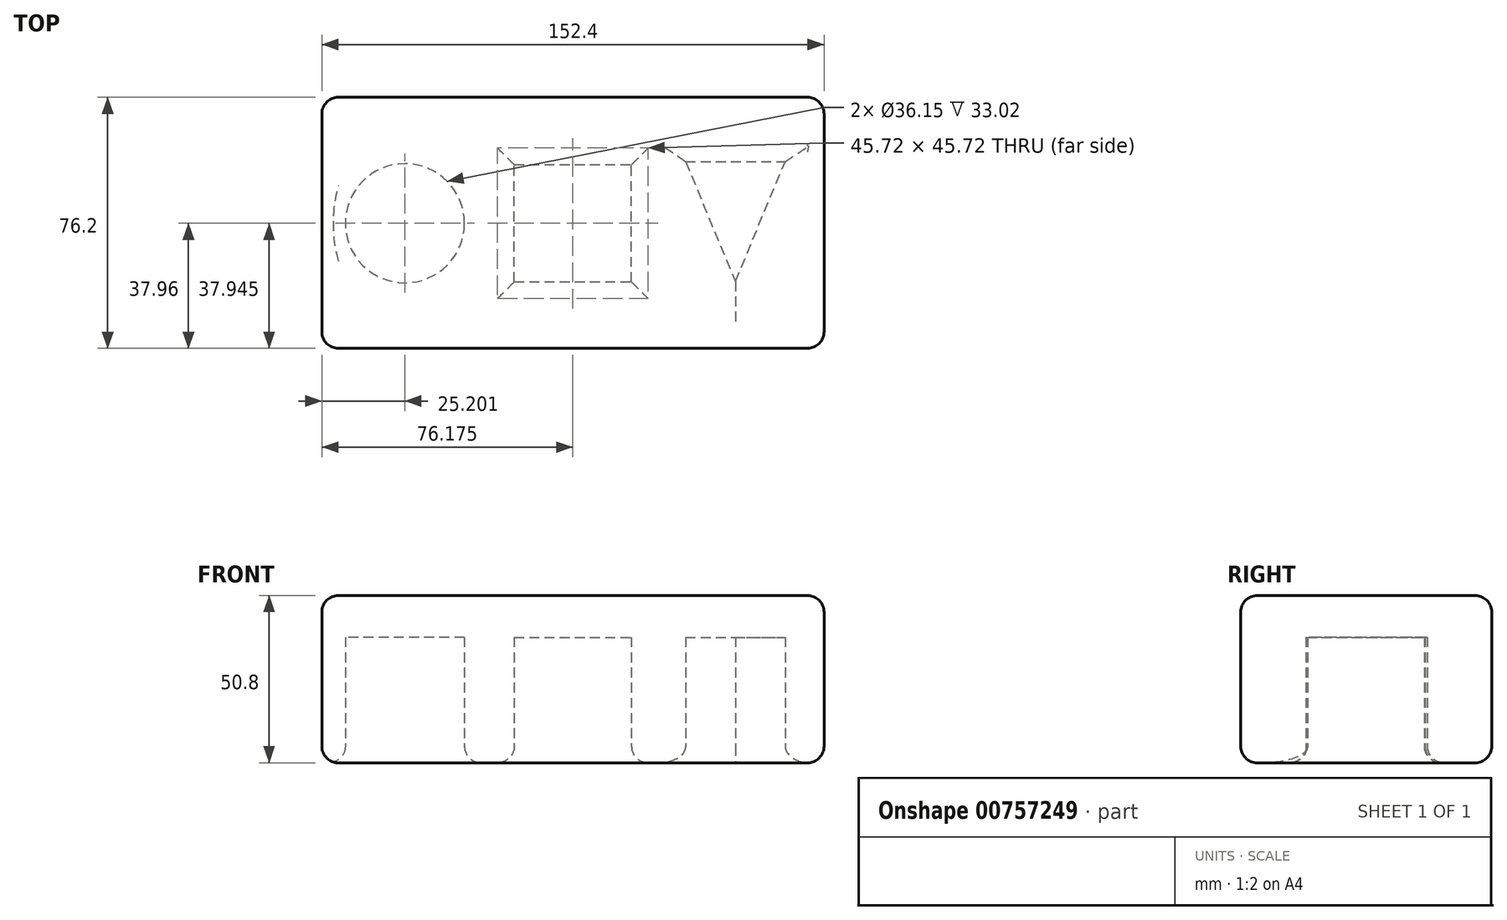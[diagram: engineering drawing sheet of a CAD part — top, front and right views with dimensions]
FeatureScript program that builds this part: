
annotation { "Feature Type Name" : "Feature", "Feature Type Description" : "" }
export const myFeature = defineFeature(function(context is Context, id is Id, definition is map)
    precondition{}
    {
        {
            var Q0;
            Q0=qCreatedBy(makeId("Top.planeOp"),FACE);
            var sketch = newSketch(context, id + "F0", { "sketchPlane" : qUnion([Q0])});
            skLineSegment(sketch, "E0.bottom", {"start": v(-74.7, 38.24) * mm, "end": v(77.7, 38.24) * mm});
            skLineSegment(sketch, "E0.top", {"start": v(-74.7, -37.96) * mm, "end": v(77.7, -37.96) * mm});
            skLineSegment(sketch, "E0.left", {"start": v(-74.7, 38.24) * mm, "end": v(-74.7, -37.96) * mm});
            skLineSegment(sketch, "E0.right", {"start": v(77.7, 38.24) * mm, "end": v(77.7, -37.96) * mm});
            skSolve(sketch);
        }
        {
            var Q0;
            Q0 = qSketchRegion(id + "F0", true);
            extrude(context, id + "F1", {"entities" : qUnion([Q0]), "depth" : 50.8 * mm, "offsetDistance" : 25.4 * mm});
        }
        {
            var Q0;
            Q0=qCreatedBy(makeId("Top.planeOp"),FACE);
            var sketch = newSketch(context, id + "F2", { "sketchPlane" : qUnion([Q0])});
            skCircle(sketch, "E1", {"center": v(-49.5, 0) * mm, "radius": 18.07 * mm});
            skSolve(sketch);
        }
        {
            var Q0;
            Q0 = qSketchRegion(id + "F2", true);
            extrude(context, id + "F3", {"entities" : qUnion([Q0]), "operationType" : NewBodyOperationType.REMOVE, "depth" : 38.1 * mm, "offsetDistance" : 25.4 * mm});
        }
        {
            var Q0;
            Q0=qCreatedBy(makeId("Top.planeOp"),FACE);
            var sketch = newSketch(context, id + "F4", { "sketchPlane" : qUnion([Q0])});
            skLineSegment(sketch, "E2.bottom", {"start": v(-16.3, -17.8) * mm, "end": v(19.25, -17.8) * mm});
            skLineSegment(sketch, "E2.top", {"start": v(-16.3, 17.77) * mm, "end": v(19.25, 17.77) * mm});
            skLineSegment(sketch, "E2.left", {"start": v(-16.3, -17.8) * mm, "end": v(-16.3, 17.77) * mm});
            skLineSegment(sketch, "E2.right", {"start": v(19.25, -17.8) * mm, "end": v(19.25, 17.77) * mm});
            skSolve(sketch);
        }
        {
            var Q0;
            Q0=qCreatedBy(makeId("Top.planeOp"),FACE);
            var sketch = newSketch(context, id + "F5", { "sketchPlane" : qUnion([Q0])});
            skLineSegment(sketch, "E3", {"start": v(35.67, 18.71) * mm, "end": v(65.9, 18.71) * mm});
            skLineSegment(sketch, "E4", {"start": v(35.67, 18.71) * mm, "end": v(50.79, -17.6) * mm});
            skLineSegment(sketch, "E5", {"start": v(50.79, -17.6) * mm, "end": v(65.9, 18.71) * mm});
            skLineSegment(sketch, "E6", {"start": v(50.79, 18.71) * mm, "end": v(50.79, -17.6) * mm});
            skSolve(sketch);
        }
        {
            var Q0;
            Q0 = qSketchRegion(id + "F5", true);
            extrude(context, id + "F6", {"entities" : qUnion([Q0]), "operationType" : NewBodyOperationType.REMOVE, "depth" : 38.1 * mm, "offsetDistance" : 25.4 * mm});
        }
        {
            var Q0;
            Q0 = qSketchRegion(id + "F4", true);
            extrude(context, id + "F7", {"entities" : qUnion([Q0]), "operationType" : NewBodyOperationType.REMOVE, "depth" : 38.1 * mm, "offsetDistance" : 25.4 * mm});
        }
        {
            var Q0;
            Q0=makeQuery(id+"F3.boolean.opBoolean","COPY",EDGE,{"derivedFrom":makeQuery(id+"F3.opExtrude","CAP_EDGE",EDGE,{"disambiguationData":[OSD([sQuery(id+"F2.wireOp",EDGE,"E1")])],"isStart":true})});
            var Q1;
            Q1=makeQuery(id+"F7.boolean.opBoolean","COPY",EDGE,{"derivedFrom":makeQuery(id+"F7.opExtrude","CAP_EDGE",EDGE,{"disambiguationData":[OSD([sQuery(id+"F4.wireOp",EDGE,"E2.bottom")])],"isStart":true})});
            var Q2;
            Q2=makeQuery(id+"F7.boolean.opBoolean","COPY",EDGE,{"derivedFrom":makeQuery(id+"F7.opExtrude","CAP_EDGE",EDGE,{"disambiguationData":[OSD([sQuery(id+"F4.wireOp",EDGE,"E2.left")])],"isStart":true})});
            var Q3;
            Q3=makeQuery(id+"F7.boolean.opBoolean","COPY",EDGE,{"derivedFrom":makeQuery(id+"F7.opExtrude","CAP_EDGE",EDGE,{"disambiguationData":[OSD([sQuery(id+"F4.wireOp",EDGE,"E2.top")])],"isStart":true})});
            var Q4;
            Q4=makeQuery(id+"F7.boolean.opBoolean","COPY",EDGE,{"derivedFrom":makeQuery(id+"F7.opExtrude","CAP_EDGE",EDGE,{"disambiguationData":[OSD([sQuery(id+"F4.wireOp",EDGE,"E2.right")])],"isStart":true})});
            var Q5;
            Q5=makeQuery(id+"F6.boolean.opBoolean","COPY",EDGE,{"derivedFrom":makeQuery(id+"F6.opExtrude","CAP_EDGE",EDGE,{"disambiguationData":[OSD([sQuery(id+"F5.wireOp",EDGE,"E4")])],"isStart":true})});
            var Q6;
            Q6=makeQuery(id+"F6.boolean.opBoolean","COPY",EDGE,{"derivedFrom":makeQuery(id+"F6.opExtrude","CAP_EDGE",EDGE,{"disambiguationData":[OSD([sQuery(id+"F5.wireOp",EDGE,"E5")])],"isStart":true})});
            var Q7;
            Q7=makeQuery(id+"F6.boolean.opBoolean","COPY",EDGE,{"derivedFrom":makeQuery(id+"F6.opExtrude","CAP_EDGE",EDGE,{"disambiguationData":[OSD([sQuery(id+"F5.wireOp",EDGE,"E3")])],"isStart":true})});
            var Q8;
            Q8=makeQuery(id+"F1.opExtrude","CAP_FACE",FACE,{"disambiguationData":[OSD([sQuery(id+"F0.wireOp",EDGE,"E0.bottom"),sQuery(id+"F0.wireOp",EDGE,"E0.top"),sQuery(id+"F0.wireOp",EDGE,"E0.left"),sQuery(id+"F0.wireOp",EDGE,"E0.right")])],"isStart":true});
            var Q9;
            Q9=makeQuery(id+"F1.opExtrude","SWEPT_EDGE",EDGE,{"disambiguationData":[OSD([sQuery(id+"F0.wireOp",EDGE,"E0.bottom"),sQuery(id+"F0.wireOp",EDGE,"E0.right")])]});
            var Q10;
            Q10=makeQuery(id+"F1.opExtrude","SWEPT_EDGE",EDGE,{"disambiguationData":[OSD([sQuery(id+"F0.wireOp",EDGE,"E0.top"),sQuery(id+"F0.wireOp",EDGE,"E0.right")])]});
            var Q11;
            Q11=makeQuery(id+"F1.opExtrude","SWEPT_EDGE",EDGE,{"disambiguationData":[OSD([sQuery(id+"F0.wireOp",EDGE,"E0.top"),sQuery(id+"F0.wireOp",EDGE,"E0.left")])]});
            var Q12;
            Q12=makeQuery(id+"F1.opExtrude","SWEPT_EDGE",EDGE,{"disambiguationData":[OSD([sQuery(id+"F0.wireOp",EDGE,"E0.bottom"),sQuery(id+"F0.wireOp",EDGE,"E0.left")])]});
            var Q13;
            Q13=makeQuery(id+"F1.opExtrude","CAP_EDGE",EDGE,{"disambiguationData":[OSD([sQuery(id+"F0.wireOp",EDGE,"E0.bottom")])],"isStart":false});
            var Q14;
            Q14=makeQuery(id+"F1.opExtrude","CAP_EDGE",EDGE,{"disambiguationData":[OSD([sQuery(id+"F0.wireOp",EDGE,"E0.top")])],"isStart":false});
            var Q15;
            Q15=makeQuery(id+"F1.opExtrude","CAP_FACE",FACE,{"disambiguationData":[OSD([sQuery(id+"F0.wireOp",EDGE,"E0.bottom"),sQuery(id+"F0.wireOp",EDGE,"E0.top"),sQuery(id+"F0.wireOp",EDGE,"E0.left"),sQuery(id+"F0.wireOp",EDGE,"E0.right")])],"isStart":false});
            fillet(context, id + "F8", {"entities" : qUnion([Q0, Q1, Q2, Q3, Q4, Q5, Q6, Q7, Q8, Q9, Q10, Q11, Q12, Q13, Q14, Q15]), "radius" : 5.08 * mm, "tangentPropagation" : true, "allowEdgeOverflow" : false});
        }
    });
